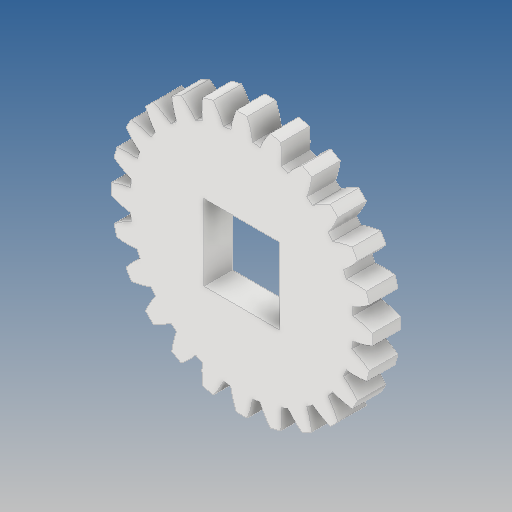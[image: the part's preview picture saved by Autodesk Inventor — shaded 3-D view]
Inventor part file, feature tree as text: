
AUTODESK INVENTOR PART (.ipt)
format: ipt  version: 2017 (Build 210142000, 142)  size: 230,912 bytes
history: native  units: mm
features: other x6, extrude x1, sketch x1, reference x1
ambient origin geometry x8: Origin, YZ Plane, XZ Plane, XY Plane, X Axis, Y Axis, Z Axis, Center Point
bodies: Body1 (feature_tree)
feature tree (9):
  other  "Sólido1"
  extrude  "Extrusión1"  Depth=6.0mm TaperAngle=0.0deg
  other  "Dientes de engranaje recto1"
  sketch  "Boceto1"  dims[d0=55.0mm d1=6.0mm d2=0.0mm]
  reference  "Referencia1"
  other  "iFeature1:1"
  other  "<userpath>\Dropbox\E\Caja Motriz\transmision Engranajes\Polea Compuesta.iam"
  other  "Polea Compuesta.iam"
  other  "dado polea:1"
